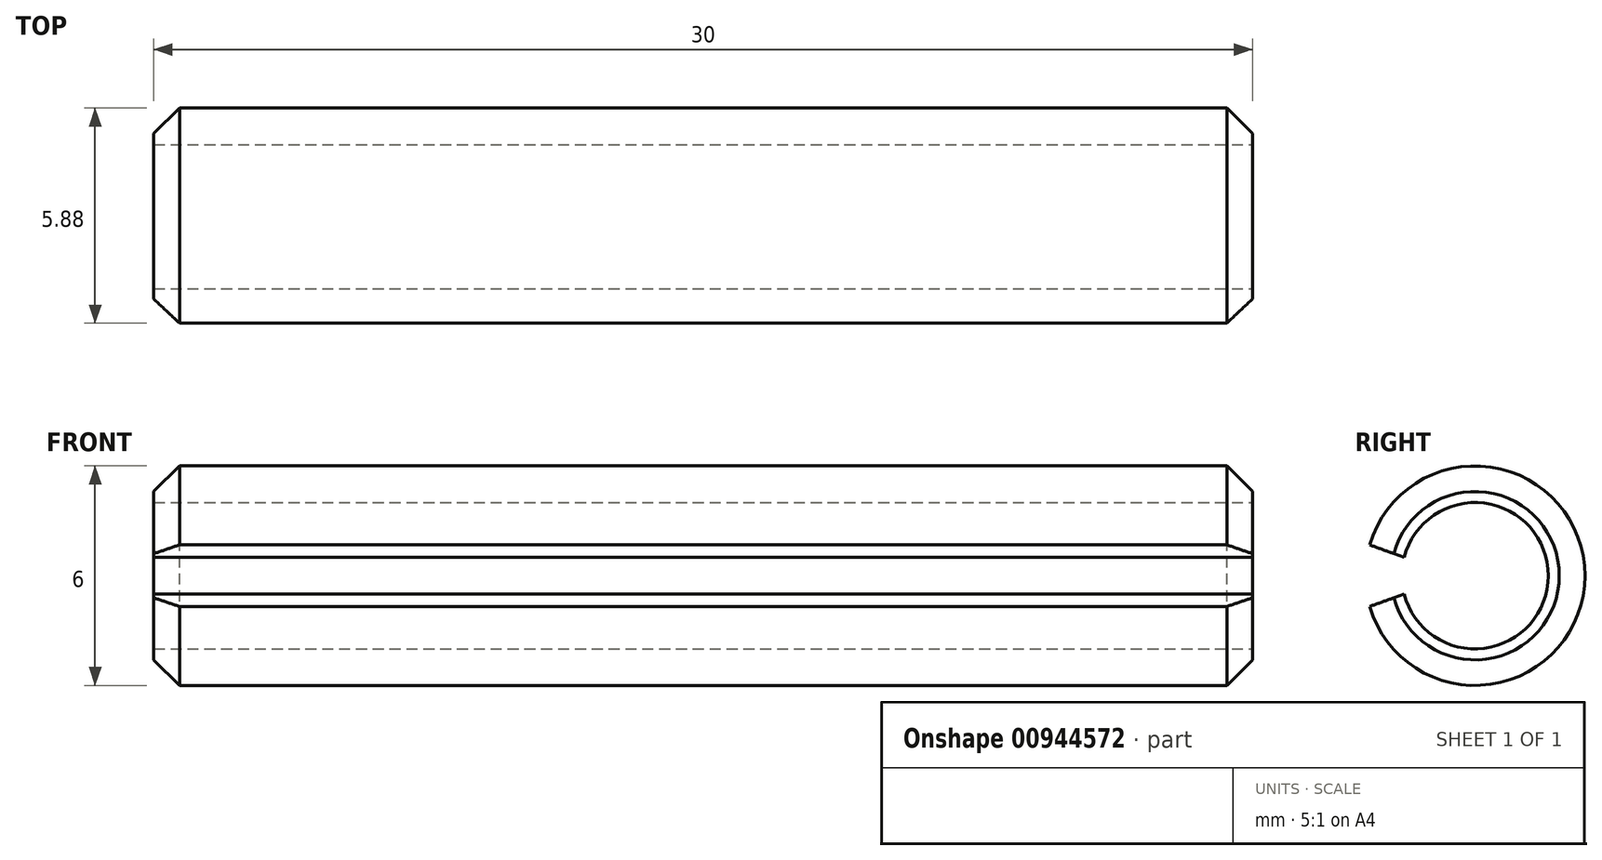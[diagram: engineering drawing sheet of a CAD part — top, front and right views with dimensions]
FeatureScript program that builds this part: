
annotation { "Feature Type Name" : "Feature", "Feature Type Description" : "" }
export const myFeature = defineFeature(function(context is Context, id is Id, definition is map)
    precondition{}
    {
        {
            var Q0;
            Q0=qCreatedBy(makeId("Right.planeOp"),FACE);
            var sketch = newSketch(context, id + "F0", { "sketchPlane" : qUnion([Q0])});
            skCircle(sketch, "E0", {"center": v(0, 0) * mm, "radius": 3 * mm});
            skSolve(sketch);
        }
        {
            var Q0;
            Q0 = qSketchRegion(id + "F0", true);
            extrude(context, id + "F1", {"entities" : qUnion([Q0]), "depth" : 30 * mm, "offsetDistance" : 25 * mm});
        }
        {
            var Q0;
            Q0=makeQuery(id+"F1.opExtrude","CAP_EDGE",EDGE,{"disambiguationData":[OSD([sQuery(id+"F0.wireOp",EDGE,"E0")])],"isStart":false});
            var Q1;
            Q1=makeQuery(id+"F1.opExtrude","CAP_EDGE",EDGE,{"disambiguationData":[OSD([sQuery(id+"F0.wireOp",EDGE,"E0")])],"isStart":true});
            chamfer(context, id + "F2", {"entities" : qUnion([Q0, Q1]), "width" : 0.7 * mm, "tangentPropagation" : true});
        }
        {
            var Q0;
            Q0=makeQuery(id+"F1.opExtrude","CAP_FACE",FACE,{"disambiguationData":[OSD([sQuery(id+"F0.wireOp",EDGE,"E0")])],"isStart":false});
            var sketch = newSketch(context, id + "F3", { "sketchPlane" : qUnion([Q0])});
            skArc(sketch, "E1", {"start": v(-1.94, -0.5) * mm, "mid": v(2, 0) * mm, "end": v(-1.94, 0.5) * mm});
            skLineSegment(sketch, "E2", {"start": v(-1.94, 0.5) * mm, "end": v(-3.31, 1) * mm});
            skLineSegment(sketch, "E3", {"start": v(-3.31, 1) * mm, "end": v(-3.31, -1) * mm});
            skLineSegment(sketch, "E4", {"start": v(-3.31, -1) * mm, "end": v(-1.94, -0.5) * mm});
            skLineSegment(sketch, "E5", {"start": v(0, 0) * mm, "end": v(-4.8, 0) * mm, "construction": true});
            skSolve(sketch);
        }
        {
            var Q0;
            {var subQ0=sQuery(id+"F3.wireOp",EDGE,"E3");Q0=makeQuery(id+"F3.imprint","IMPRINT",FACE,{"disambiguationData":[TD([[makeQuery(id+"F3.imprint","IMPRINT",EDGE,{"derivedFrom":subQ0}),1.0]])]});}
            var Q1;
            {var subQ0=sQuery(id+"F3.wireOp",EDGE,"E1");Q1=makeQuery(id+"F3.imprint","IMPRINT",FACE,{"disambiguationData":[TD([[makeQuery(id+"F3.imprint","IMPRINT",EDGE,{"derivedFrom":subQ0}),1.0]])]});}
            extrude(context, id + "F4", {"entities" : qUnion([Q0, Q1]), "operationType" : NewBodyOperationType.REMOVE, "oppositeDirection" : true, "depth" : 31 * mm, "offsetDistance" : 25 * mm});
        }
    });
